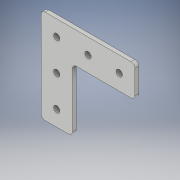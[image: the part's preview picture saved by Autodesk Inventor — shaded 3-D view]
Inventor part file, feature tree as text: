
AUTODESK INVENTOR PART (.ipt)
format: ipt  version: 2018 (Build 220112000, 112)  size: 129,024 bytes
history: native  units: in
note: dims shown in document units (in); Inventor stores cm internally (conversion verified against a paired STEP export)
features: extrude x2, sketch x2, fillet x1
ambient origin geometry x8: Origin, YZ Plane, XZ Plane, XY Plane, X Axis, Y Axis, Z Axis, Center Point
bodies: Solid1 (feature_tree)
feature tree (5):
  extrude  "Extrusion1"  Depth=3.0in
  extrude  "Extrusion2"  Depth=1.0in
  fillet  "Fillet1"  Radius=0.125in
  sketch  "Sketch1"  dims[d0=1.0in d1=3.0in]
  sketch  "Sketch2"  dims[d2=3.0in d3=1.0in d4=0.125in d5=0.0in d6=0.5in d7=1.0in d8=1.0in d11=1.0in d12=1.0in d13=0.2031in d14=0.125in d15=0.0in d16=0.125in]
